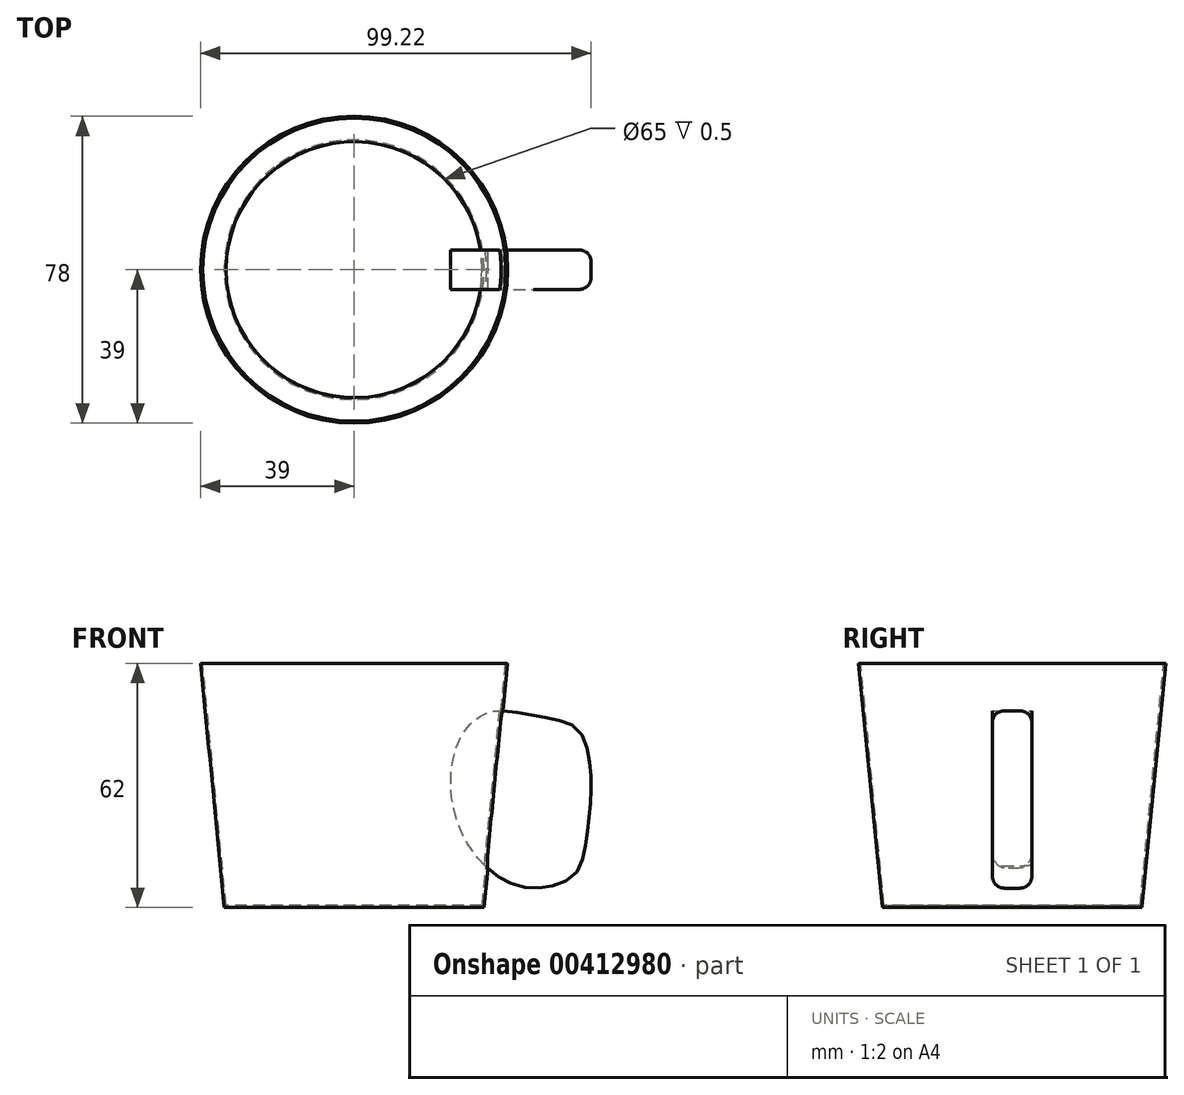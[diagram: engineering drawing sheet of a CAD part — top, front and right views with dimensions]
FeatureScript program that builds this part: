
annotation { "Feature Type Name" : "Feature", "Feature Type Description" : "" }
export const myFeature = defineFeature(function(context is Context, id is Id, definition is map)
    precondition{}
    {
        {
            var Q0;
            Q0=qCreatedBy(makeId("Right.planeOp"),FACE);
            var sketch = newSketch(context, id + "F0", { "sketchPlane" : qUnion([Q0])});
            skLineSegment(sketch, "E0", {"start": v(0, 0) * mm, "end": v(0, 62) * mm});
            skLineSegment(sketch, "E1", {"start": v(0, 62) * mm, "end": v(39, 62) * mm});
            skLineSegment(sketch, "E2", {"start": v(39, 62) * mm, "end": v(33, 0) * mm});
            skLineSegment(sketch, "E3", {"start": v(33, 0) * mm, "end": v(0, 0) * mm});
            skSolve(sketch);
        }
        {
            var Q0;
            Q0=makeQuery(id+"F0.imprint","IMPRINT",FACE,{"disambiguationData":[TD([[makeQuery(id+"F0.imprint","IMPRINT",EDGE,{"derivedFrom":sQuery(id+"F0.wireOp",EDGE,"E0")}),-1.0]])]});
            var Q1;
            Q1=sQuery(id+"F0.wireOp",EDGE,"E0");
            revolve(context, id + "F1", {"entities" : qUnion([Q0]), "axis" : qUnion([Q1]), "revolveType" : RevolveType.FULL});
        }
        {
            var Q0;
            Q0=makeQuery(id+"F1.opRevolve","SWEPT_FACE",FACE,{"disambiguationData":[OSD([sQuery(id+"F0.wireOp",EDGE,"E1")])]});
            shell(context, id + "F2", {"entities" : qUnion([Q0]), "thickness" : .5 * mm});
        }
        {
            var Q0;
            Q0=makeQuery(id+"F1.opRevolve","SWEPT_FACE",FACE,{"disambiguationData":[OSD([sQuery(id+"F0.wireOp",EDGE,"E3")])]});
            var sketch = newSketch(context, id + "F3", { "sketchPlane" : qUnion([Q0])});
            skCircle(sketch, "E4", {"center": v(0, 0) * mm, "radius": 32.5 * mm});
            skSolve(sketch);
        }
        {
            var Q0;
            Q0 = qSketchRegion(id + "F3", true);
            extrude(context, id + "F4", {"entities" : qUnion([Q0]), "operationType" : NewBodyOperationType.REMOVE, "endBound" : BoundingType.THROUGH_ALL, "oppositeDirection" : true, "depth" : 25 * mm});
        }
        {
            var Q0;
            Q0=qCreatedBy(makeId("Front.planeOp"),FACE);
            var sketch = newSketch(context, id + "F5", { "sketchPlane" : qUnion([Q0])});
            skFitSpline(sketch, "E5", {"points": [v(37.75, 49.91) * mm, v(50.1, 47.88) * mm, v(57.28, 44.76) * mm, v(60.16, 32.9) * mm, v(59.68, 22.71) * mm, v(57.52, 10.73) * mm, v(55.49, 7.85) * mm, v(52.49, 6.06) * mm, v(42.54, 5.22) * mm, v(30.68, 13.48) * mm, v(24.69, 28.82) * mm, v(27.2, 43.44) * mm, v(32.84, 48.95) * mm, v(37.75, 49.91) * mm]});
            skFitSpline(sketch, "E6.0", {"points": [v(36.6, 44.93) * mm, v(37.4, 44.94) * mm, v(39, 44.8) * mm, v(40.97, 44.52) * mm, v(43.16, 44.14) * mm, v(45.08, 43.77) * mm, v(46.6, 43.47) * mm, v(47.74, 43.24) * mm, v(48.66, 43.06) * mm, v(49.38, 42.92) * mm, v(50.06, 42.79) * mm, v(50.83, 42.63) * mm, v(51.6, 42.46) * mm, v(52.23, 42.29) * mm, v(52.68, 42.13) * mm, v(52.98, 42) * mm, v(53.14, 41.9) * mm, v(53.2, 41.84) * mm, v(53.26, 41.79) * mm, v(53.3, 41.74) * mm, v(53.35, 41.67) * mm, v(53.43, 41.55) * mm, v(53.53, 41.38) * mm, v(53.68, 41.08) * mm, v(53.88, 40.6) * mm, v(54.13, 39.9) * mm, v(54.35, 39.05) * mm, v(54.63, 37.82) * mm, v(54.9, 36.12) * mm, v(55.07, 34.35) * mm, v(55.15, 32.98) * mm, v(55.2, 31.66) * mm, v(55.23, 30.15) * mm, v(55.17, 28.44) * mm, v(55.08, 27) * mm, v(54.97, 25.77) * mm, v(54.88, 24.8) * mm, v(54.77, 23.8) * mm, v(54.65, 22.71) * mm, v(54.52, 21.6) * mm, v(54.34, 20.07) * mm, v(54.08, 18.16) * mm, v(53.73, 15.98) * mm, v(53.4, 14.4) * mm, v(53.18, 13.51) * mm, v(53.05, 13.08) * mm, v(52.96, 12.8) * mm, v(52.88, 12.58) * mm, v(52.79, 12.36) * mm, v(52.7, 12.17) * mm, v(52.62, 12.05) * mm, v(52.57, 11.98) * mm, v(52.5, 11.9) * mm, v(52.42, 11.82) * mm, v(52.34, 11.75) * mm, v(52.25, 11.67) * mm, v(52.16, 11.6) * mm, v(52.08, 11.52) * mm, v(52, 11.45) * mm, v(51.85, 11.34) * mm, v(51.7, 11.22) * mm, v(51.49, 11.1) * mm, v(51.24, 10.96) * mm, v(50.92, 10.81) * mm, v(50.5, 10.64) * mm, v(49.96, 10.46) * mm, v(49.33, 10.3) * mm, v(48.42, 10.09) * mm, v(47.16, 9.9) * mm, v(45.83, 9.85) * mm, v(44.8, 9.91) * mm, v(44.17, 10) * mm, v(43.68, 10.08) * mm, v(43.2, 10.2) * mm, v(42.6, 10.37) * mm, v(41.84, 10.65) * mm, v(40.82, 11.11) * mm, v(39.53, 11.86) * mm, v(37.99, 13) * mm, v(36.5, 14.36) * mm, v(35.1, 15.9) * mm, v(33.83, 17.6) * mm, v(32.72, 19.4) * mm, v(31.43, 21.95) * mm, v(30.48, 24.67) * mm, v(29.87, 27.5) * mm, v(29.51, 30.38) * mm, v(29.53, 33.34) * mm, v(29.9, 36.12) * mm, v(30.27, 37.72) * mm, v(30.63, 38.88) * mm, v(30.93, 39.68) * mm, v(31.2, 40.28) * mm, v(31.42, 40.72) * mm, v(31.64, 41.13) * mm, v(31.94, 41.6) * mm, v(32.32, 42.13) * mm, v(32.72, 42.61) * mm, v(33.27, 43.2) * mm, v(33.84, 43.68) * mm, v(34.4, 44.08) * mm, v(34.74, 44.3) * mm, v(35, 44.44) * mm, v(35.19, 44.54) * mm, v(35.36, 44.62) * mm, v(35.55, 44.7) * mm, v(35.75, 44.78) * mm, v(35.95, 44.84) * mm, v(36.19, 44.89) * mm, v(36.6, 44.93) * mm, v(37.4, 44.94) * mm, v(39, 44.8) * mm]});
            skLineSegment(sketch, "E7", {"start": v(37.75, 49.91) * mm, "end": v(37.27, 44.93) * mm});
            skLineSegment(sketch, "E8.trimOffspring", {"start": v(34.53, 16.69) * mm, "end": v(33.88, 10) * mm});
            skSolve(sketch);
        }
        {
            var Q0;
            Q0 = qSketchRegion(id + "F5", true);
            extrude(context, id + "F6", {"entities" : qUnion([Q0]), "operationType" : NewBodyOperationType.ADD, "endBound" : BoundingType.SYMMETRIC, "depth" : 10 * mm});
        }
        {
            var Q0;
            {var subQ0=sQuery(id+"F5.wireOp",EDGE,"E5");Q0=makeQuery(id+"F6.boolean.opBoolean","SPLIT",EDGE,{"disambiguationData":[TD([makeQuery(id+"F1.opRevolve","SWEPT_FACE",FACE,{"disambiguationData":[OSD([sQuery(id+"F0.wireOp",EDGE,"E2")])]})])],"derivedFrom":makeQuery(id+"F6.opExtrude","CAP_EDGE",EDGE,{"disambiguationData":[OSD([subQ0])],"isStart":false})});}
            var Q1;
            {var subQ0=sQuery(id+"F5.wireOp",EDGE,"E6.0");Q1=makeQuery(id+"F6.boolean.opBoolean","SPLIT",EDGE,{"disambiguationData":[TD([makeQuery(id+"F1.opRevolve","SWEPT_FACE",FACE,{"disambiguationData":[OSD([sQuery(id+"F0.wireOp",EDGE,"E2")])]})])],"derivedFrom":makeQuery(id+"F6.opExtrude","CAP_EDGE",EDGE,{"disambiguationData":[OSD([subQ0])],"isStart":false})});}
            var Q2;
            {var subQ0=sQuery(id+"F5.wireOp",EDGE,"E5");Q2=makeQuery(id+"F6.boolean.opBoolean","SPLIT",EDGE,{"disambiguationData":[TD([makeQuery(id+"F1.opRevolve","SWEPT_FACE",FACE,{"disambiguationData":[OSD([sQuery(id+"F0.wireOp",EDGE,"E2")])]})])],"derivedFrom":makeQuery(id+"F6.opExtrude","CAP_EDGE",EDGE,{"disambiguationData":[OSD([subQ0])],"isStart":true})});}
            var Q3;
            {var subQ0=sQuery(id+"F5.wireOp",EDGE,"E6.0");Q3=makeQuery(id+"F6.boolean.opBoolean","SPLIT",EDGE,{"disambiguationData":[TD([makeQuery(id+"F1.opRevolve","SWEPT_FACE",FACE,{"disambiguationData":[OSD([sQuery(id+"F0.wireOp",EDGE,"E2")])]})])],"derivedFrom":makeQuery(id+"F6.opExtrude","CAP_EDGE",EDGE,{"disambiguationData":[OSD([subQ0])],"isStart":true})});}
            fillet(context, id + "F7", {"entities" : qUnion([Q0, Q1, Q2, Q3]), "radius" : 3 * mm, "tangentPropagation" : true, "allowEdgeOverflow" : false});
        }
    });
